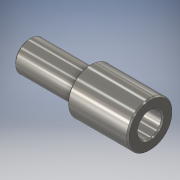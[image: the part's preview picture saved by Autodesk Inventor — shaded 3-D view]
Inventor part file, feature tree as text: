
AUTODESK INVENTOR PART (.ipt)
format: ipt  version: 2016 (Build 200138000, 138)  size: 154,112 bytes
history: native  units: in
note: dims shown in document units (in); Inventor stores cm internally (conversion verified against a paired STEP export)
features: extrude x3, sketch x3, chamfer x1
ambient origin geometry x8: Origin, YZ Plane, XZ Plane, XY Plane, X Axis, Y Axis, Z Axis, Center Point
bodies: Solid1 (feature_tree)
feature tree (7):
  extrude  "Extrusion1"  Depth=0.5in TaperAngle=0.0deg
  extrude  "Extrusion2"  Depth=0.5in TaperAngle=0.0deg
  extrude  "Extrusion3"  Depth=0.5in
  chamfer  "Chamfer1"  Distance=0.5in
  sketch  "Sketch1"  dims[d0=0.25in d1=0.5in d2=0.0in]
  sketch  "Sketch2"  dims[d3=0.375in d4=0.5in d5=0.0in]
  sketch  "Sketch4"  dims[d6=0.2in d7=0.125in d8=0.5in d9=0.0in d10=0.01in d11=0.125in d12=45.0deg]
